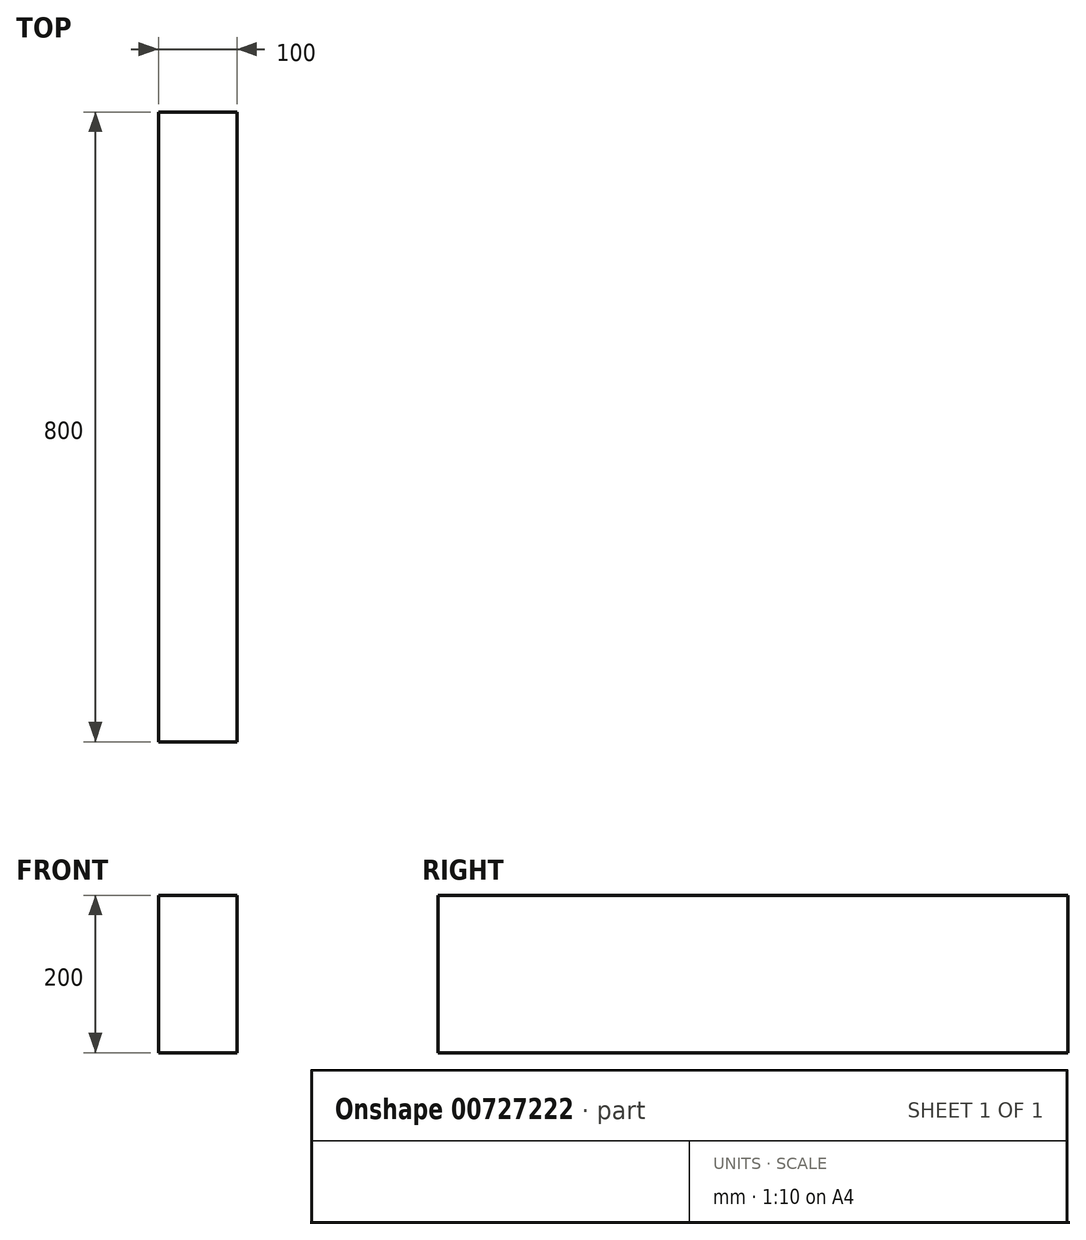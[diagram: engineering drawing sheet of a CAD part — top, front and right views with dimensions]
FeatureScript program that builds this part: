
annotation { "Feature Type Name" : "Feature", "Feature Type Description" : "" }
export const myFeature = defineFeature(function(context is Context, id is Id, definition is map)
    precondition{}
    {
        {
            var Q0;
            Q0=qCreatedBy(makeId("Front.planeOp"),FACE);
            var sketch = newSketch(context, id + "F0", { "sketchPlane" : qUnion([Q0])});
            skLineSegment(sketch, "E0.bottom", {"start": v(-50.05, 200) * mm, "end": v(49.95, 200) * mm});
            skLineSegment(sketch, "E0.top", {"start": v(-50.05, 0) * mm, "end": v(49.95, 0) * mm});
            skLineSegment(sketch, "E0.left", {"start": v(-50.05, 200) * mm, "end": v(-50.05, 0) * mm});
            skLineSegment(sketch, "E0.right", {"start": v(49.95, 200) * mm, "end": v(49.95, 0) * mm});
            skSolve(sketch);
        }
        {
            var Q0;
            Q0=makeQuery(id+"F0.imprint","IMPRINT",FACE,{"disambiguationData":[TD([[makeQuery(id+"F0.imprint","IMPRINT",EDGE,{"derivedFrom":sQuery(id+"F0.wireOp",EDGE,"E0.bottom")}),-1.0]])]});
            var Q1;
            Q1=sQuery(id+"F0.wireOp",EDGE,"E0.left");
            var Q2;
            Q2=sQuery(id+"F0.wireOp",EDGE,"E0.bottom");
            var Q3;
            Q3=sQuery(id+"F0.wireOp",EDGE,"E0.top");
            var Q4;
            Q4=sQuery(id+"F0.wireOp",EDGE,"E0.right");
            extrude(context, id + "F1", {"entities" : qUnion([Q0]), "surfaceEntities" : qUnion([Q1, Q2, Q3, Q4]), "endBound" : BoundingType.SYMMETRIC, "depth" : 800 * mm, "offsetDistance" : 25.4 * mm});
        }
    });
